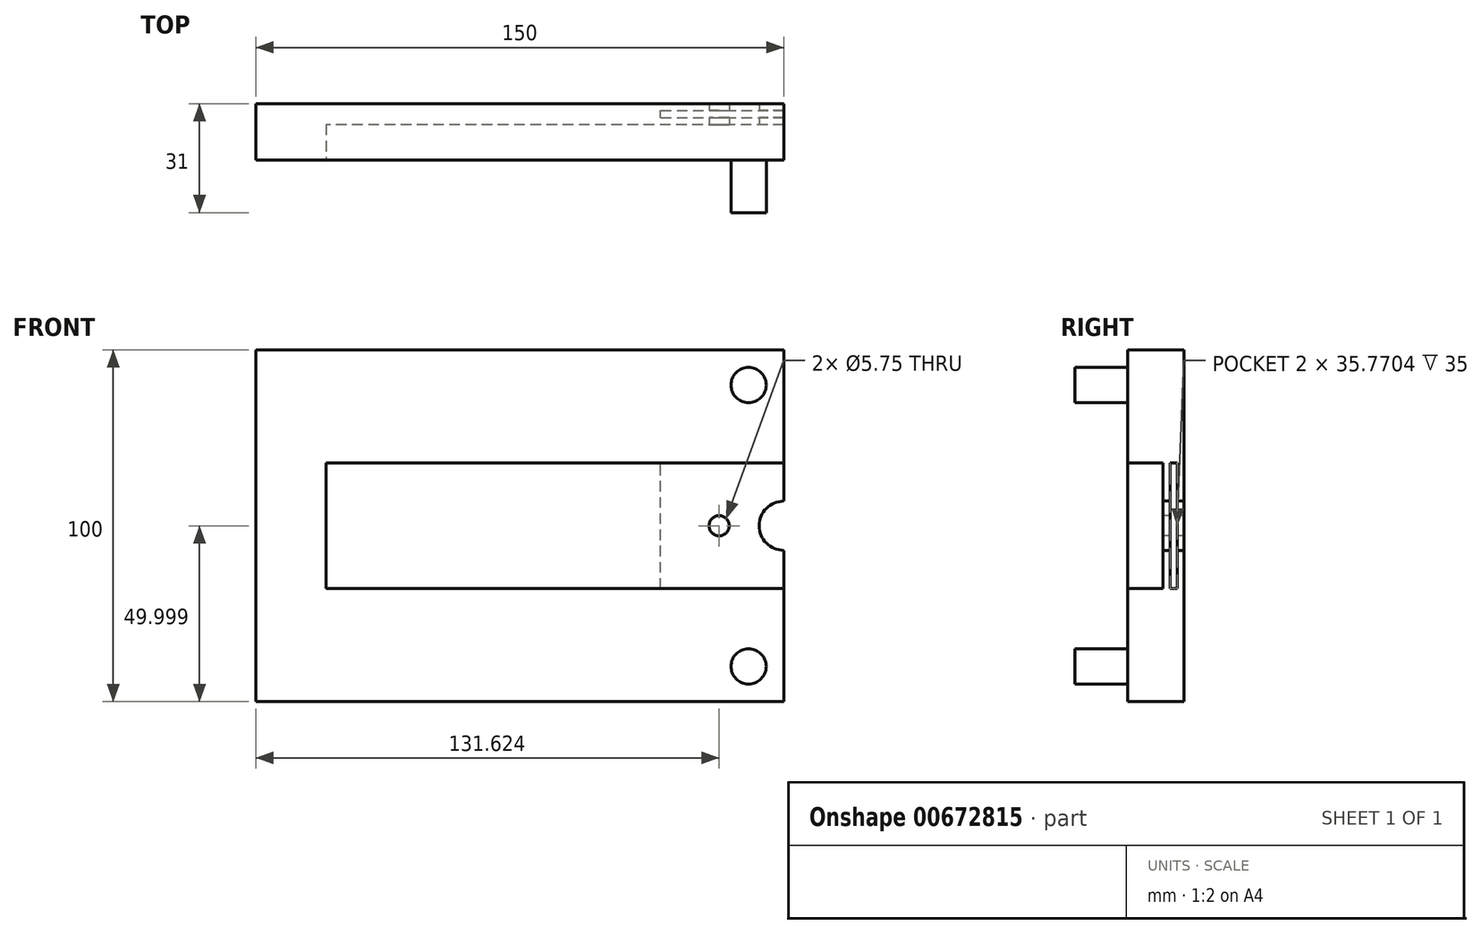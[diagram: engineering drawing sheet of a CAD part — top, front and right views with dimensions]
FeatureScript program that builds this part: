
annotation { "Feature Type Name" : "Feature", "Feature Type Description" : "" }
export const myFeature = defineFeature(function(context is Context, id is Id, definition is map)
    precondition{}
    {
        {
            var Q0;
            Q0=qCreatedBy(makeId("Front.planeOp"),FACE);
            var sketch = newSketch(context, id + "F0", { "sketchPlane" : qUnion([Q0])});
            skLineSegment(sketch, "E0.bottom", {"start": v(-276.63, 95.79) * mm, "end": v(-126.63, 95.79) * mm});
            skLineSegment(sketch, "E0.top", {"start": v(-276.63, -4.21) * mm, "end": v(-126.63, -4.21) * mm});
            skLineSegment(sketch, "E0.left", {"start": v(-276.63, 95.79) * mm, "end": v(-276.63, -4.21) * mm});
            skLineSegment(sketch, "E0.right", {"start": v(-126.63, 95.79) * mm, "end": v(-126.63, -4.21) * mm});
            skSolve(sketch);
        }
        {
            var Q0;
            Q0 = qSketchRegion(id + "F0", true);
            extrude(context, id + "F1", {"entities" : qUnion([Q0]), "depth" : 16 * mm, "offsetDistance" : 25 * mm});
        }
        {
            var Q0;
            Q0=makeQuery(id+"F1.opExtrude","CAP_FACE",FACE,{"disambiguationData":[OSD([sQuery(id+"F0.wireOp",EDGE,"E0.bottom"),sQuery(id+"F0.wireOp",EDGE,"E0.top"),sQuery(id+"F0.wireOp",EDGE,"E0.left"),sQuery(id+"F0.wireOp",EDGE,"E0.right")])],"isStart":false});
            var sketch = newSketch(context, id + "F2", { "sketchPlane" : qUnion([Q0])});
            skCircle(sketch, "E1", {"center": v(-136.63, 85.79) * mm, "radius": 5 * mm});
            skCircle(sketch, "E2", {"center": v(-136.63, 5.79) * mm, "radius": 5 * mm});
            skSolve(sketch);
        }
        {
            var Q0;
            Q0=makeQuery(id+"F2.imprint","IMPRINT",FACE,{"disambiguationData":[TD([[makeQuery(id+"F2.imprint","IMPRINT",EDGE,{"derivedFrom":sQuery(id+"F2.wireOp",EDGE,"E1")}),1.0]])]});
            var Q1;
            Q1=makeQuery(id+"F2.imprint","IMPRINT",FACE,{"disambiguationData":[TD([[makeQuery(id+"F2.imprint","IMPRINT",EDGE,{"derivedFrom":sQuery(id+"F2.wireOp",EDGE,"E2")}),1.0]])]});
            extrude(context, id + "F3", {"entities" : qUnion([Q0, Q1]), "operationType" : NewBodyOperationType.ADD, "depth" : 15 * mm, "offsetDistance" : 25 * mm});
        }
        {
            var Q0;
            Q0=makeQuery(id+"F1.opExtrude","CAP_FACE",FACE,{"disambiguationData":[OSD([sQuery(id+"F0.wireOp",EDGE,"E0.bottom"),sQuery(id+"F0.wireOp",EDGE,"E0.top"),sQuery(id+"F0.wireOp",EDGE,"E0.left"),sQuery(id+"F0.wireOp",EDGE,"E0.right")])],"isStart":false});
            var sketch = newSketch(context, id + "F4", { "sketchPlane" : qUnion([Q0])});
            skLineSegment(sketch, "E3", {"start": v(-126.63, 63.67) * mm, "end": v(-256.63, 63.67) * mm});
            skLineSegment(sketch, "E4", {"start": v(-256.63, 63.67) * mm, "end": v(-256.63, 27.9) * mm});
            skLineSegment(sketch, "E5", {"start": v(-256.63, 27.9) * mm, "end": v(-126.63, 27.9) * mm});
            skLineSegment(sketch, "E6", {"start": v(-126.63, 27.9) * mm, "end": v(-126.63, 63.67) * mm});
            skLineSegment(sketch, "E7", {"start": v(-177.9, 63.67) * mm, "end": v(-177.9, 95.79) * mm, "construction": true});
            skLineSegment(sketch, "E8", {"start": v(-177.9, 27.9) * mm, "end": v(-177.9, -4.21) * mm, "construction": true});
            skSolve(sketch);
        }
        {
            var Q0;
            Q0 = qSketchRegion(id + "F4", true);
            extrude(context, id + "F5", {"entities" : qUnion([Q0]), "operationType" : NewBodyOperationType.REMOVE, "oppositeDirection" : true, "depth" : 10 * mm, "offsetDistance" : 25 * mm});
        }
        {
            var Q0;
            Q0=makeQuery(id+"F5.boolean.opBoolean","COPY",FACE,{"derivedFrom":makeQuery(id+"F5.opExtrude","CAP_FACE",FACE,{"disambiguationData":[OSD([sQuery(id+"F4.wireOp",EDGE,"E3"),sQuery(id+"F4.wireOp",EDGE,"E4"),sQuery(id+"F4.wireOp",EDGE,"E5"),sQuery(id+"F4.wireOp",EDGE,"E6")])],"isStart":false})});
            var sketch = newSketch(context, id + "F6", { "sketchPlane" : qUnion([Q0])});
            skCircle(sketch, "E9", {"center": v(-145, 45.79) * mm, "radius": 2.87 * mm});
            skPoint(sketch, "E9.centerSnap0", {"position": v(-126.63, 45.79) * mm});
            skCircle(sketch, "E10", {"center": v(-126.63, 45.79) * mm, "radius": 7 * mm});
            skSolve(sketch);
        }
        {
            var Q0;
            Q0=makeQuery(id+"F6.imprint","IMPRINT",FACE,{"disambiguationData":[TD([[makeQuery(id+"F6.imprint","IMPRINT",EDGE,{"derivedFrom":sQuery(id+"F6.wireOp",EDGE,"E9")}),1.0]])]});
            var Q1;
            {var subQ0=sQuery(id+"F6.wireOp",EDGE,"E10");var subQ1=makeQuery(id+"F5.boolean.opBoolean","COPY",EDGE,{"derivedFrom":makeQuery(id+"F5.opExtrude","CAP_EDGE",EDGE,{"disambiguationData":[OSD([sQuery(id+"F4.wireOp",EDGE,"E6")])],"isStart":false})});var subQ2=makeQuery(id+"F6.imprint","INTERSECT",VERTEX,{"disambiguationData":[OD(0.0)],"derivedFrom":[subQ1,subQ0]});Q1=makeQuery(id+"F6.imprint","IMPRINT",FACE,{"disambiguationData":[TD([[makeQuery(id+"F6.imprint","IMPRINT",EDGE,{"disambiguationData":[TD([[subQ2,1.0]])],"derivedFrom":subQ0}),1.0]])]});}
            var Q2;
            {var subQ0=sQuery(id+"F6.wireOp",EDGE,"E10");var subQ1=makeQuery(id+"F5.boolean.opBoolean","COPY",EDGE,{"derivedFrom":makeQuery(id+"F5.opExtrude","CAP_EDGE",EDGE,{"disambiguationData":[OSD([sQuery(id+"F4.wireOp",EDGE,"E6")])],"isStart":false})});var subQ2=makeQuery(id+"F6.imprint","INTERSECT",VERTEX,{"disambiguationData":[OD(0.0)],"derivedFrom":[subQ1,subQ0]});Q2=makeQuery(id+"F6.imprint","IMPRINT",FACE,{"disambiguationData":[TD([[makeQuery(id+"F6.imprint","IMPRINT",EDGE,{"disambiguationData":[TD([[subQ2,-1.0]])],"derivedFrom":subQ0}),1.0]])]});}
            extrude(context, id + "F7", {"entities" : qUnion([Q0, Q1, Q2]), "operationType" : NewBodyOperationType.REMOVE, "oppositeDirection" : true, "depth" : 7 * mm, "offsetDistance" : 25 * mm});
        }
        {
            var Q0;
            Q0=makeQuery(id+"F1.opExtrude","SWEPT_FACE",FACE,{"disambiguationData":[OSD([sQuery(id+"F0.wireOp",EDGE,"E0.right")])]});
            var sketch = newSketch(context, id + "F8", { "sketchPlane" : qUnion([Q0])});
            skLineSegment(sketch, "E11", {"start": v(-4, 27.9) * mm, "end": v(-2, 27.9) * mm});
            skLineSegment(sketch, "E12", {"start": v(-2, 27.9) * mm, "end": v(-2, 63.67) * mm});
            skLineSegment(sketch, "E13", {"start": v(-2, 63.67) * mm, "end": v(-4, 63.67) * mm});
            skLineSegment(sketch, "E14", {"start": v(-4, 63.67) * mm, "end": v(-4, 27.9) * mm});
            skSolve(sketch);
        }
        {
            var Q0;
            {var subQ0=sQuery(id+"F8.wireOp",EDGE,"E11");Q0=makeQuery(id+"F8.imprint","IMPRINT",FACE,{"disambiguationData":[TD([[makeQuery(id+"F8.imprint","IMPRINT",EDGE,{"derivedFrom":subQ0}),1.0]])]});}
            var Q1;
            {var subQ0=sQuery(id+"F8.wireOp",EDGE,"E12");var subQ1=makeQuery(id+"F7.opExtrude","SWEPT_FACE",FACE,{"disambiguationData":[OSD([sQuery(id+"F6.wireOp",EDGE,"E10")])]});var subQ2=makeQuery(id+"F1.opExtrude","SWEPT_FACE",FACE,{"disambiguationData":[OSD([sQuery(id+"F0.wireOp",EDGE,"E0.right")])]});var subQ3=makeQuery(id+"F7.boolean.opBoolean","INTERSECT",EDGE,{"disambiguationData":[OD(1.0)],"derivedFrom":[subQ2,subQ1]});var subQ4=makeQuery(id+"F8.imprint","INTERSECT",VERTEX,{"derivedFrom":[subQ3,subQ0]});Q1=makeQuery(id+"F8.imprint","IMPRINT",FACE,{"disambiguationData":[TD([[makeQuery(id+"F8.imprint","IMPRINT",EDGE,{"disambiguationData":[TD([[subQ4,-1.0]])],"derivedFrom":subQ0}),1.0]])]});}
            var Q2;
            {var subQ0=sQuery(id+"F8.wireOp",EDGE,"E13");Q2=makeQuery(id+"F8.imprint","IMPRINT",FACE,{"disambiguationData":[TD([[makeQuery(id+"F8.imprint","IMPRINT",EDGE,{"derivedFrom":subQ0}),1.0]])]});}
            extrude(context, id + "F9", {"entities" : qUnion([Q0, Q1, Q2]), "operationType" : NewBodyOperationType.REMOVE, "oppositeDirection" : true, "depth" : 35 * mm, "offsetDistance" : 25 * mm});
        }
    });
